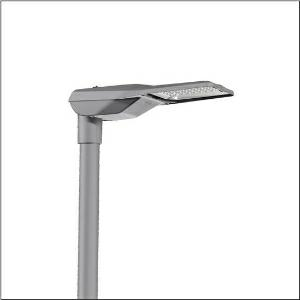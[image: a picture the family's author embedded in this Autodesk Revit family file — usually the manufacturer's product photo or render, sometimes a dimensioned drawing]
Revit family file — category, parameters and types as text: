
# Revit family: streetlight_sl_21_iq_mini___st1_0a_5xe2d31v08hb_a16f
name_source: partatom
category: Lighting Fixtures
units: mm (PartAtom-declared; Revit-internal decimal feet)

## family parameters
Cut with Voids When Loaded = No
Host = Face
Light Source = No
Part Type = Normal
Room Calculation Point = No
Round Connector Dimension = Use Diameter
Shared = No

## types (1)
- --- (1 x LED, 9750 lm, 71 W, 3000K)
    Apparent Load = 71 VA
    CIE Flux Codes = 37 72 97 100 100
    Color Rendering = 70
    Color Temperature = 3000K
    Default Elevation = 1800 mm
    Description = Streetlight SL 21 iQ mini, mast luminaire, primary light control with lens, of PMMA, primary optical cover: cover, of toughened safety glass, transparent, light distribution: ST1.0a, light emission: direct distribution, primary light characteristic: asymmetric, installation type: post-top, side-entry, LED, High Power LED, rated luminous flux: 9.750lm, luminous efficacy: 137lm/W, light colour: 730, colour temperature: 3000K, control gear: iQ-Street Remote, D4i with power reduction, control: pre-setting: logarithmic dimming characteristic, Street-Remote, Auto-Match, Temp-Guard, Lumen-Switch, Night-Set, Smart-Wire, Light-Fading, Desk-Remote (wireless, voltage-free reading and setting of iQ features in the workshop via application-optimized NFC function/RFID function), optimised constant luminous flux control (CLO 2.0), mains connection: 220..240V, AC, 50/60Hz, start of lifetime: 71W, end of service life: 75W, reduction: 30W, luminaire housing, of diecast aluminium, powder-coated, SITECO metallic grey (DB 702S), corrosivity category C5 high according to DIN EN ISO 12944, please order mast flange separately, inclination adjustable: 0°, 5°, 10°, 15°, sealing non-destructively replaceable, multi-level sealing system, length: 628mm, width: 235mm, height: 110mm, mast flange for spigot size: 42mm (side-entry): 5XC10008XM4, 60/48mm (side-entry/post-top): 5XC10108XM2, 76/60mm (side-entry/post-top): 5XC10108XM1, mounting height: 4..8m, Smart Interface above, protection rating (complete): IP66, insulation class (complete): insulation class II (safety insulation), certification: CE, ENEC, ENEC+, VDE, impact resistance: IK10, permissible operating ambient temperature for outdoor applications: -40..+50°C, standard-compliant lighting for roads and squares, packaging unit: 1 piece

Light Distribution: ST1.0a
    Height = 110 mm
    Lamp = 1 x LED
    Lamp Light Flux = 9750 lm
    Lamp Power = 71 W
    Lamp count = 1
    Length = 625 mm
    Luminous efficacy = 137 lm/W
    Manufacturer = Siteco
    ModVariant = No
    Model = 5XE2D31V08HB
    Number of Poles = 1
    OnlyDefault = Yes
    Power Factor = 1
    Product Name = Streetlight SL 21 iQ mini | ST1.0a
    Product group = mast luminaire | pylon top
    ProductGroupID = 6100
    Protection Class = Protection class II
    Protection Degree = IP 66
    RLX_Detail_Level = 1
    RLX_Emergency_Light_Flux = 0 lm
    RLX_Emergency_Type = 0
    RLX_Emergency_Type_DB = No
    RlxData = <blob elided: 92389 chars, md5=61289122>
    Socket = socket
    Standby Power = 0 W
    System Light Flux = 9750 lm
    System Power = 71 W
    Type Comments = factory setting: luminous flux: 100 % | dim-lin: 254 | 716 mA
    Type Image = l_1003515.jpg
    URL = http://relux.com
    VarID = @adj_115233
    Voltage = 0 V
    Weight = 0.00 kg
    Width = 234 mm

## geometry (parser evidence)
native form markers: Blend x4, Sweep x11
no freeform markers — native parametric forms only
